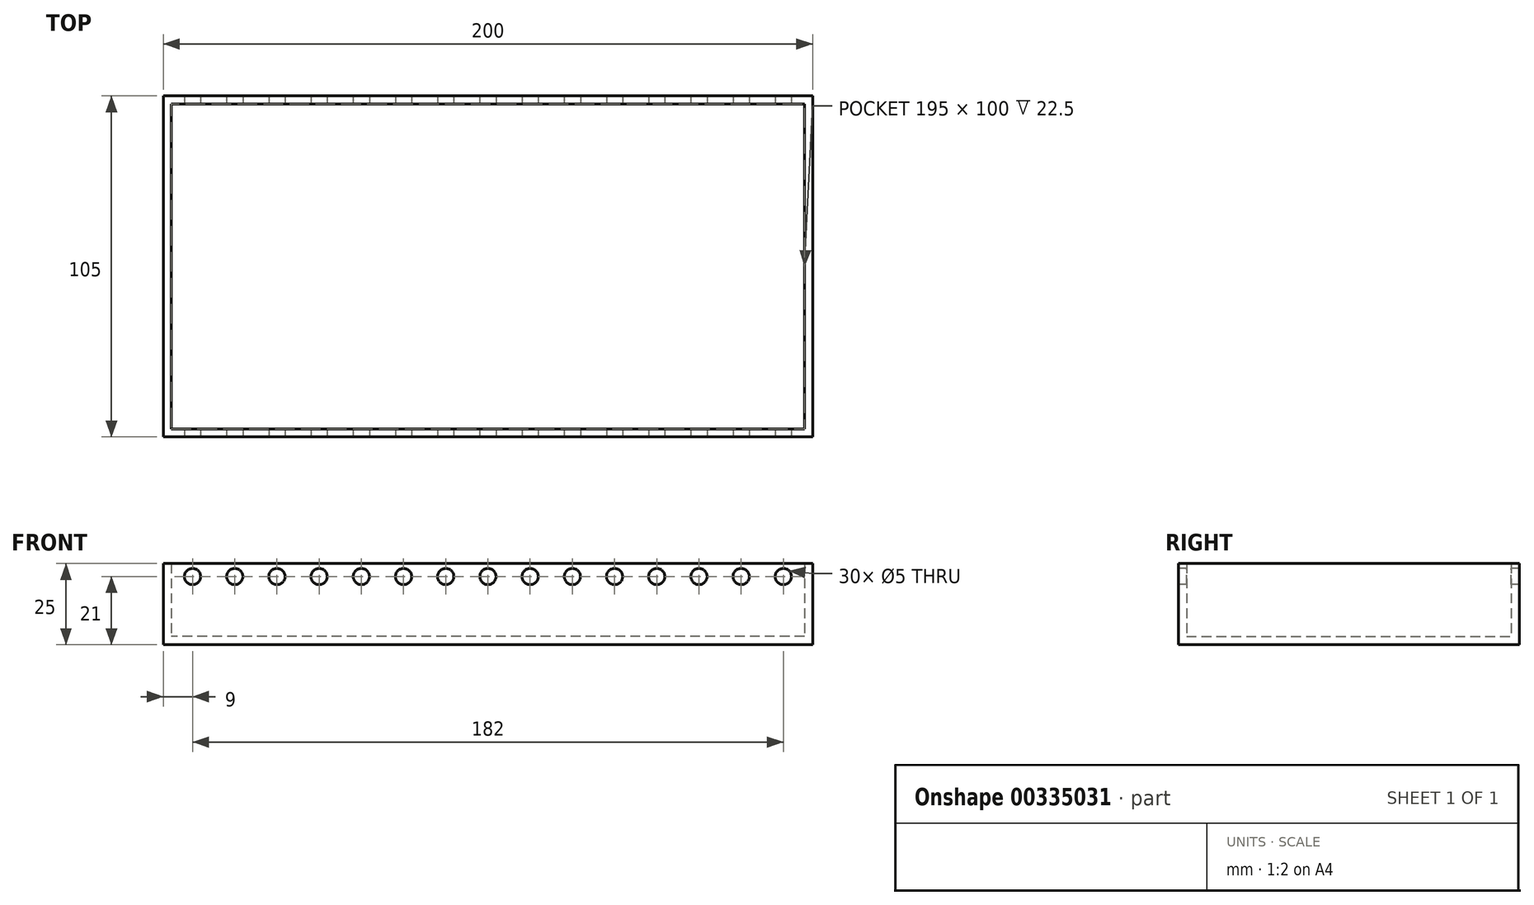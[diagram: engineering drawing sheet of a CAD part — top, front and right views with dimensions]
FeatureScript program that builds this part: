
annotation { "Feature Type Name" : "Feature", "Feature Type Description" : "" }
export const myFeature = defineFeature(function(context is Context, id is Id, definition is map)
    precondition{}
    {
        {
            var Q0;
            Q0=qCreatedBy(makeId("Top.planeOp"),FACE);
            var sketch = newSketch(context, id + "F0", { "sketchPlane" : qUnion([Q0])});
            skLineSegment(sketch, "E0.bottom", {"start": v(100, -52.5) * mm, "end": v(-100, -52.5) * mm});
            skLineSegment(sketch, "E0.top", {"start": v(100, 52.5) * mm, "end": v(-100, 52.5) * mm});
            skLineSegment(sketch, "E0.left", {"start": v(100, -52.5) * mm, "end": v(100, 52.5) * mm});
            skLineSegment(sketch, "E0.right", {"start": v(-100, -52.5) * mm, "end": v(-100, 52.5) * mm});
            skPoint(sketch, "E0.middle", {"position": v(0, 0) * mm});
            skSolve(sketch);
        }
        {
            var Q0;
            Q0=makeQuery(id+"F0.imprint","IMPRINT",FACE,{"disambiguationData":[TD([[makeQuery(id+"F0.imprint","IMPRINT",EDGE,{"derivedFrom":sQuery(id+"F0.wireOp",EDGE,"E0.bottom")}),-1.0]])]});
            extrude(context, id + "F1", {"entities" : qUnion([Q0]), "depth" : 25 * mm});
        }
        {
            var Q0;
            Q0=makeQuery(id+"F1.opExtrude","CAP_FACE",FACE,{"disambiguationData":[OSD([sQuery(id+"F0.wireOp",EDGE,"E0.bottom"),sQuery(id+"F0.wireOp",EDGE,"E0.top"),sQuery(id+"F0.wireOp",EDGE,"E0.left"),sQuery(id+"F0.wireOp",EDGE,"E0.right")])],"isStart":false});
            shell(context, id + "F2", {"entities" : qUnion([Q0]), "thickness" : 2.5 * mm});
        }
        {
            var Q0;
            Q0=makeQuery(id+"F1.opExtrude","SWEPT_FACE",FACE,{"disambiguationData":[OSD([sQuery(id+"F0.wireOp",EDGE,"E0.bottom")])]});
            var sketch = newSketch(context, id + "F3", { "sketchPlane" : qUnion([Q0])});
            skLineSegment(sketch, "E1", {"start": v(0, 25) * mm, "end": v(0, 21) * mm, "construction": true});
            skPoint(sketch, "E1.endSnap0", {"position": v(0, 25) * mm});
            skCircle(sketch, "E2.2.0.0", {"center": v(-91, 21) * mm, "radius": 2.5 * mm});
            skCircle(sketch, "E3.1.0.0", {"center": v(-78, 21) * mm, "radius": 2.5 * mm});
            skCircle(sketch, "E3.2.0.0", {"center": v(-65, 21) * mm, "radius": 2.5 * mm});
            skCircle(sketch, "E3.3.0.0", {"center": v(-52, 21) * mm, "radius": 2.5 * mm});
            skCircle(sketch, "E3.4.0.0", {"center": v(-39, 21) * mm, "radius": 2.5 * mm});
            skCircle(sketch, "E3.5.0.0", {"center": v(-26, 21) * mm, "radius": 2.5 * mm});
            skLineSegment(sketch, "E3.direction1", {"start": v(-91, 21) * mm, "end": v(-78, 21) * mm, "construction": true});
            skCircle(sketch, "E4.0.6.0", {"center": v(-13, 21) * mm, "radius": 2.5 * mm});
            skCircle(sketch, "E4.0.7.0", {"center": v(0, 21) * mm, "radius": 2.5 * mm});
            skCircle(sketch, "E4.0.8.0", {"center": v(13, 21) * mm, "radius": 2.5 * mm});
            skCircle(sketch, "E4.0.9.0", {"center": v(26, 21) * mm, "radius": 2.5 * mm});
            skCircle(sketch, "E4.0.10.0", {"center": v(39, 21) * mm, "radius": 2.5 * mm});
            skCircle(sketch, "E4.0.11.0", {"center": v(52, 21) * mm, "radius": 2.5 * mm});
            skCircle(sketch, "E4.0.12.0", {"center": v(65, 21) * mm, "radius": 2.5 * mm});
            skCircle(sketch, "E4.0.13.0", {"center": v(78, 21) * mm, "radius": 2.5 * mm});
            skCircle(sketch, "E4.0.14.0", {"center": v(91, 21) * mm, "radius": 2.5 * mm});
            skSolve(sketch);
        }
        {
            var Q0;
            Q0=qSketchRegion(id+"F3",true);
            var Q1;
            Q1=makeQuery(id+"F1.opExtrude","SWEPT_FACE",FACE,{"disambiguationData":[OSD([sQuery(id+"F0.wireOp",EDGE,"E0.top")])]});
            extrude(context, id + "F4", {"entities" : qUnion([Q0]), "operationType" : NewBodyOperationType.REMOVE, "endBound" : BoundingType.UP_TO_SURFACE, "oppositeDirection" : true, "endBoundEntityFace" : qUnion([Q1]), "depth" : 138.9 * mm});
        }
    });
